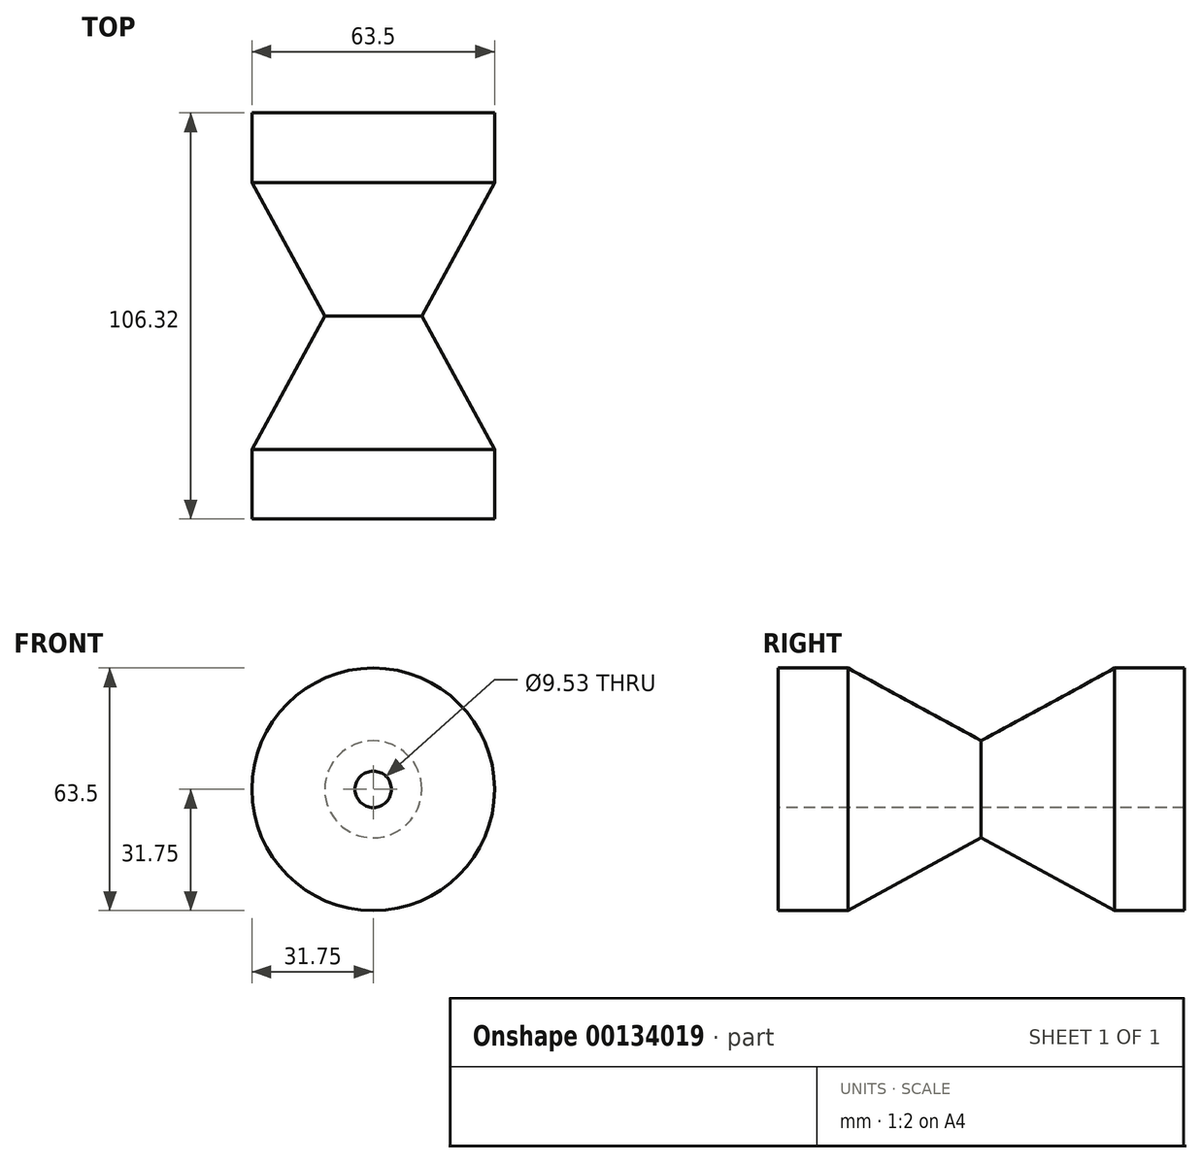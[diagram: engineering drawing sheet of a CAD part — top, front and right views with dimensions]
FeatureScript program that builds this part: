
annotation { "Feature Type Name" : "Feature", "Feature Type Description" : "" }
export const myFeature = defineFeature(function(context is Context, id is Id, definition is map)
    precondition{}
    {
        {
            var Q0;
            Q0=qCreatedBy(makeId("Front.planeOp"),FACE);
            var sketch = newSketch(context, id + "F0", { "sketchPlane" : qUnion([Q0])});
            skCircle(sketch, "E0", {"center": v(0, 0) * mm, "radius": 31.75 * mm});
            skSolve(sketch);
        }
        {
            var Q0;
            Q0 = qSketchRegion(id + "F0", true);
            extrude(context, id + "F1", {"entities" : qUnion([Q0]), "endBound" : BoundingType.SYMMETRIC, "depth" : 87.27 * mm + 19.05 * mm});
        }
        {
            var Q0;
            Q0=qCreatedBy(makeId("Right.planeOp"),FACE);
            var sketch = newSketch(context, id + "F2", { "sketchPlane" : qUnion([Q0])});
            skLineSegment(sketch, "E1", {"start": v(0, 31.75) * mm, "end": v(0, 12.7) * mm});
            skLineSegment(sketch, "E2", {"start": v(0, 12.7) * mm, "end": v(34.93, 31.75) * mm});
            skLineSegment(sketch, "E3", {"start": v(34.93, 31.75) * mm, "end": v(-34.93, 31.75) * mm});
            skLineSegment(sketch, "E4", {"start": v(-34.93, 31.75) * mm, "end": v(0, 12.7) * mm});
            skLineSegment(sketch, "E5", {"start": v(-34.93, 31.75) * mm, "end": v(-53.16, 31.75) * mm, "construction": true});
            skLineSegment(sketch, "E6", {"start": v(34.93, 31.75) * mm, "end": v(53.16, 31.75) * mm, "construction": true});
            skLineSegment(sketch, "E7", {"start": v(-53.16, 0) * mm, "end": v(53.16, 0) * mm, "construction": true});
            skSolve(sketch);
        }
        {
            var Q0;
            Q0 = qSketchRegion(id + "F2", true);
            var Q1;
            Q1=sQuery(id+"F2.wireOp",EDGE,"E7");
            revolve(context, id + "F3", {"operationType" : NewBodyOperationType.REMOVE, "entities" : qUnion([Q0]), "axis" : qUnion([Q1]), "revolveType" : RevolveType.FULL, "oppositeDirection" : true});
        }
        {
            var Q0;
            Q0=makeQuery(id+"F1.opExtrude","CAP_FACE",FACE,{"disambiguationData":[OSD([sQuery(id+"F0.wireOp",EDGE,"E0")])],"isStart":false});
            var sketch = newSketch(context, id + "F4", { "sketchPlane" : qUnion([Q0])});
            skPoint(sketch, "E8", {"position": v(0, 0) * mm});
            skSolve(sketch);
        }
        {
            var Q0;
            Q0=sQuery(id+"F4.wireOp",VERTEX,"E8");
            var Q1;
            Q1=makeQuery(id+"F1.opExtrude","SWEPT_BODY",BODY,{"disambiguationData":[OSD([sQuery(id+"F0.wireOp",EDGE,"E0")])]});
            hole(context, id + "F5", {"style" : HoleStyle.SIMPLE, "endStyle" : HoleEndStyle.THROUGH, "holeDiameter" : 9.52 * mm, "locations" : qUnion([Q0]), "scope" : qUnion([Q1]), "isTappedThrough" : true});
        }
    });
